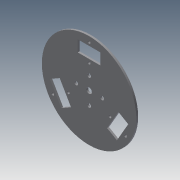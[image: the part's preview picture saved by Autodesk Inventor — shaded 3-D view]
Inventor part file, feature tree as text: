
AUTODESK INVENTOR PART (.ipt)
format: ipt  version: 2013 (Build 170138000, 138)  size: 269,312 bytes
history: native  units: mm
features: sketch x14, extrude x11
ambient origin geometry x8: Origin, YZ Plane, XZ Plane, XY Plane, X Axis, Y Axis, Z Axis, Center Point
bodies: Solid1 (feature_tree)
feature tree (25):
  extrude  "Extrusion1"  Depth=6.0mm
  extrude  "Extrusion2"  Depth=23.0mm
  extrude  "Extrusion3"  Depth=4.0mm
  extrude  "Extrusion4"  Depth=4.0mm
  extrude  "Extrusion5"  Depth=2.0mm TaperAngle=0.0deg
  extrude  "Extrusion6"  Depth=27.5mm
  extrude  "Extrusion7"  Depth=4.0mm
  extrude  "Extrusion8"  Depth=4.0mm
  sketch  "Sketch9"  dims[d30=2.0mm d31=0.0mm d35=24.0mm]
  sketch  "Sketch10"  dims[d36=10.0mm d38=10.0mm]
  extrude  "Extrusion9"  Depth=24.0mm
  extrude  "Extrusion10"  Depth=10.0mm
  sketch  "Sketch13"  dims[d45=10.0mm]
  extrude  "Extrusion11"  Depth=24.0mm
  sketch  "Sketch1"  dims[d1=2.0mm d2=0.0mm d3=6.0mm]
  sketch  "Sketch2"  dims[d4=2.0mm d5=0.0mm d15=23.0mm]
  sketch  "Sketch3"  dims[d16=40.0mm d17=4.0mm]
  sketch  "Sketch4"  dims[d18=4.0mm d19=4.0mm]
  sketch  "Sketch5"  dims[d20=4.0mm d21=2.0mm d22=0.0mm]
  sketch  "Sketch6"  dims[d23=2.0mm d24=0.0mm d25=27.5mm]
  sketch  "Sketch7"  dims[d26=4.0mm d27=4.0mm]
  sketch  "Sketch8"  dims[d28=4.0mm d29=4.0mm]
  sketch  "Sketch11"  dims[d39=12.0mm d41=24.0mm]
  sketch  "Sketch12"  dims[d44=12.0mm]
  sketch  "Sketch14"  dims[d46=24.0mm d47=10.0mm d48=2.0mm d49=0.0mm d50=24.0mm d51=14.0mm d52=7.0mm d53=24.0mm d54=14.0mm d55=24.0mm d56=7.0mm d57=24.0mm d58=14.0mm d59=24.0mm d60=2.0mm d61=0.0mm d62=24.0mm d63=12.0mm d64=6.0mm d65=24.0mm d66=12.0mm d67=24.0mm d68=6.0mm d69=24.0mm d70=12.0mm d71=2.0mm d72=0.0mm d85=2.0mm d86=0.0mm d92=12.0mm d93=12.0mm d94=12.0mm d97=12.0mm d98=2.0mm d99=0.0mm d107=3.0mm d108=3.0mm d109=3.0mm d110=3.0mm d112=3.0mm d113=2.0mm d114=0.0mm]
